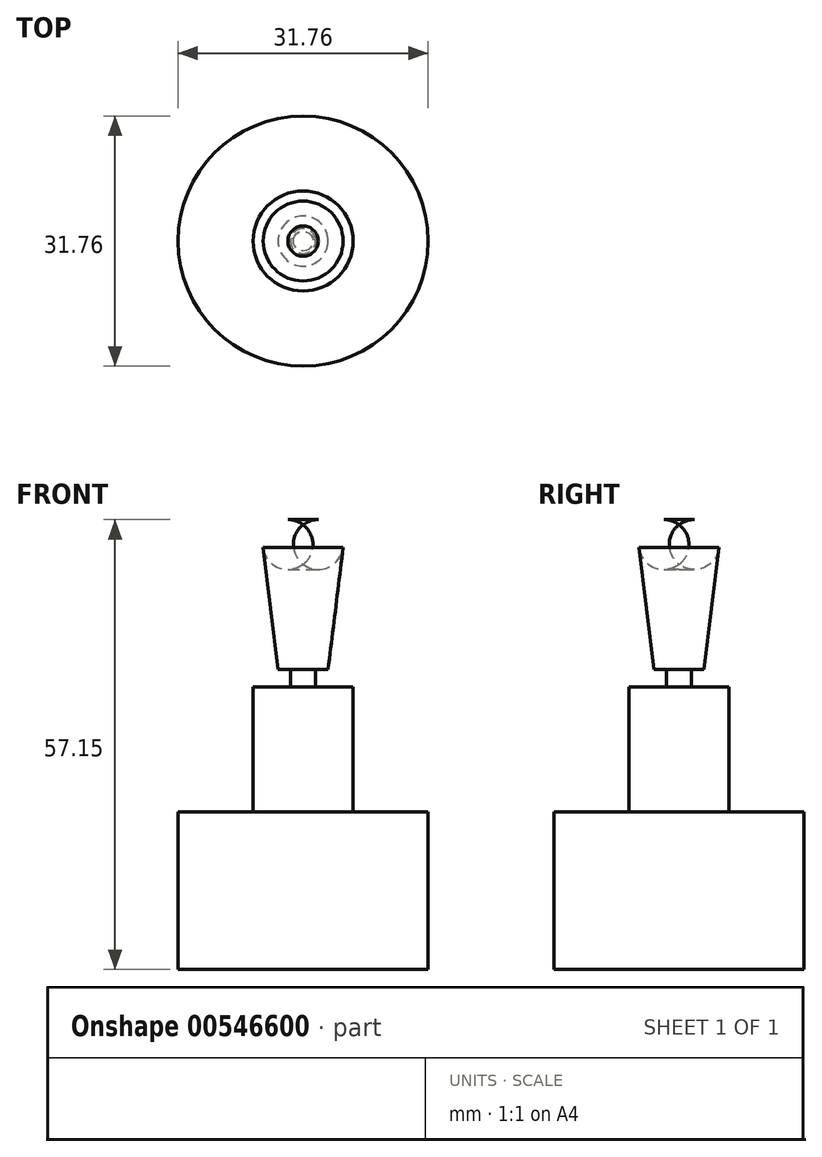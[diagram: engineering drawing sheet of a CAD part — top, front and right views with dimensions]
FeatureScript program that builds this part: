
annotation { "Feature Type Name" : "Feature", "Feature Type Description" : "" }
export const myFeature = defineFeature(function(context is Context, id is Id, definition is map)
    precondition{}
    {
        {
            var Q0;
            Q0=qCreatedBy(makeId("Front.planeOp"),FACE);
            var sketch = newSketch(context, id + "F0", { "sketchPlane" : qUnion([Q0])});
            skLineSegment(sketch, "E0", {"start": v(0, 57.15) * mm, "end": v(0, 0) * mm});
            skLineSegment(sketch, "E1", {"start": v(0, 0) * mm, "end": v(15.88, 0) * mm});
            skLineSegment(sketch, "E2", {"start": v(15.88, 0) * mm, "end": v(15.88, 20) * mm});
            skLineSegment(sketch, "E3", {"start": v(15.88, 20) * mm, "end": v(6.35, 20) * mm});
            skLineSegment(sketch, "E4", {"start": v(6.35, 20) * mm, "end": v(6.35, 35.88) * mm});
            skLineSegment(sketch, "E5", {"start": v(6.35, 35.88) * mm, "end": v(1.59, 35.88) * mm});
            skLineSegment(sketch, "E6", {"start": v(1.59, 35.88) * mm, "end": v(1.59, 38.1) * mm});
            skLineSegment(sketch, "E7", {"start": v(1.59, 38.1) * mm, "end": v(3.17, 38.1) * mm});
            skLineSegment(sketch, "E8", {"start": v(3.17, 38.1) * mm, "end": v(5.08, 53.59) * mm});
            skLineSegment(sketch, "E9", {"start": v(0, 57.15) * mm, "end": v(1.93, 57.15) * mm});
            skArc(sketch, "E10", {"start": v(5.08, 53.59) * mm, "mid": v(4.3, 56.08) * mm, "end": v(1.93, 57.15) * mm});
            skSolve(sketch);
        }
        {
            var Q0;
            Q0=qSketchRegion(id+"F0",true);
            var Q1;
            Q1=sQuery(id+"F0.wireOp",EDGE,"E0");
            revolve(context, id + "F1", {"entities" : qUnion([Q0]), "axis" : qUnion([Q1]), "revolveType" : RevolveType.FULL});
        }
    });
